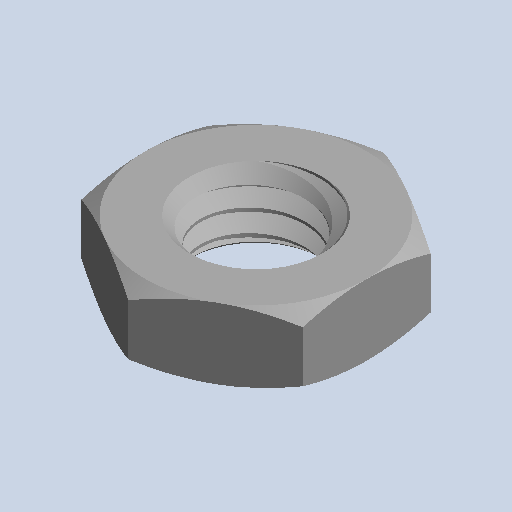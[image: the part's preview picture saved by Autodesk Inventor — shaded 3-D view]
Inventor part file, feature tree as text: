
AUTODESK INVENTOR PART (.ipt)
format: ipt  version: 2022.1 (Build 261234000, 234)  size: 203,264 bytes
history: native  units: mm (DEFAULTED — no unit token found)
features: other x8, mirror x1
bodies: Body1 (feature_tree)
feature tree (9):
  other  "Sólido1"
  other  "Origen"
  other  "Plano YZ"
  other  "Plano XZ"
  other  "Plano XY"
  other  "Eje X"
  other  "Eje Y"
  other  "Eje Z"
  mirror  "Mirror1"
